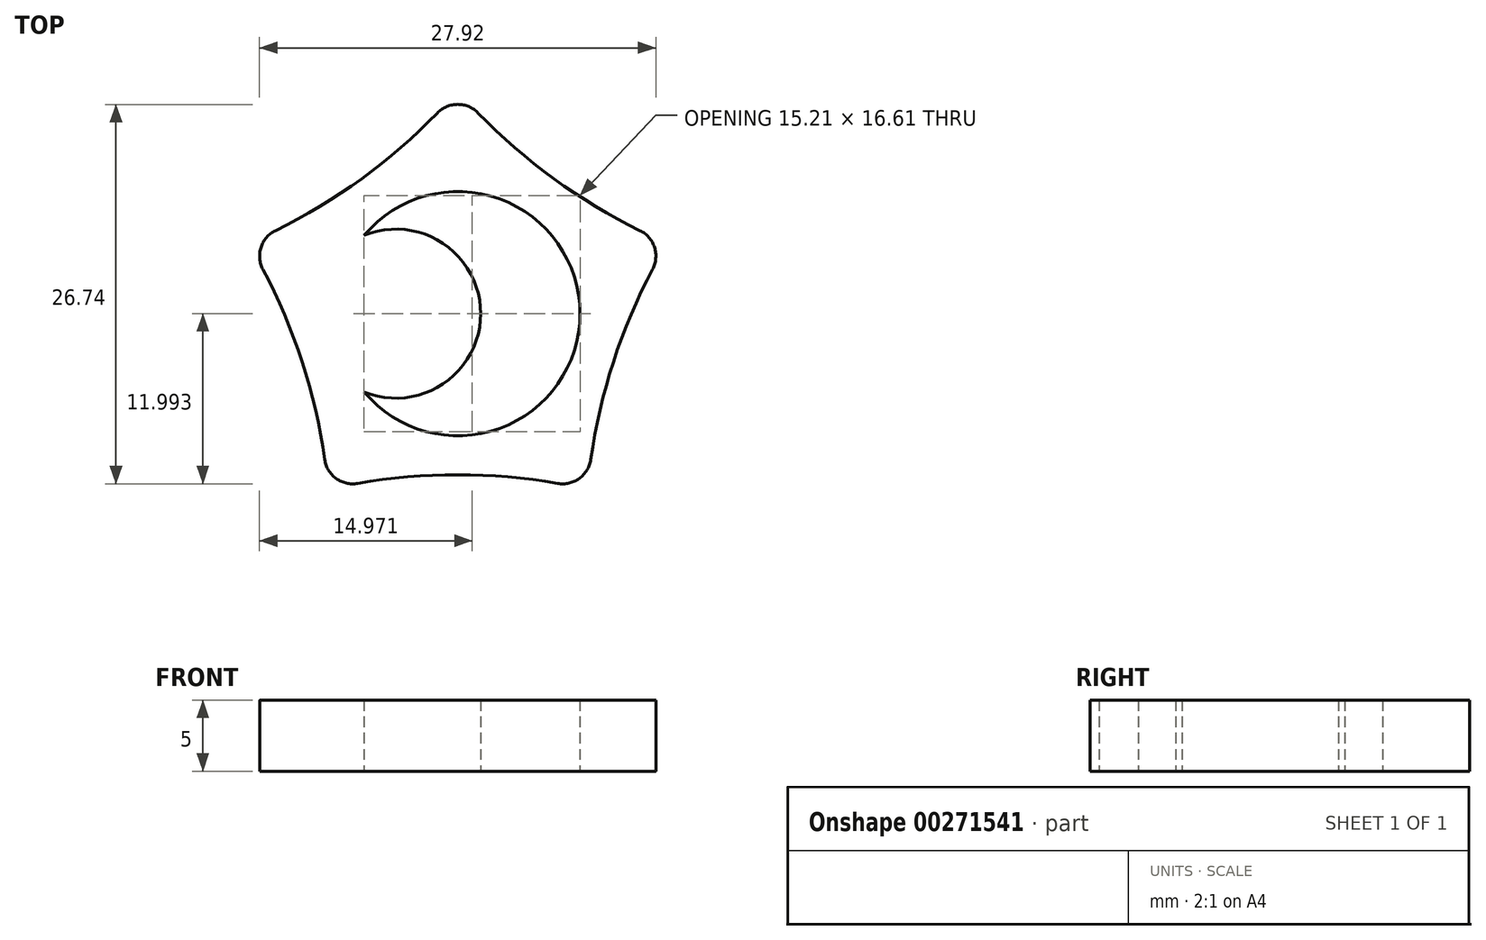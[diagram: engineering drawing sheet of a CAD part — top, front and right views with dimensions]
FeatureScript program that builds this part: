
annotation { "Feature Type Name" : "Feature", "Feature Type Description" : "" }
export const myFeature = defineFeature(function(context is Context, id is Id, definition is map)
    precondition{}
    {
        {
            var Q0;
            Q0=qCreatedBy(makeId("Top.planeOp"),FACE);
            var sketch = newSketch(context, id + "F0", { "sketchPlane" : qUnion([Q0])});
            skCircle(sketch, "E0.cCircle", {"center": v(0, 0) * mm, "radius": 12.56 * mm, "construction": true});
            skLineSegment(sketch, "E0.0", {"start": v(9.12, -12.56) * mm, "end": v(-9.12, -12.56) * mm});
            skLineSegment(sketch, "E0.1", {"start": v(-9.13, -12.56) * mm, "end": v(-14.76, 4.8) * mm});
            skLineSegment(sketch, "E0.2", {"start": v(-14.76, 4.8) * mm, "end": v(0, 15.52) * mm});
            skLineSegment(sketch, "E0.3", {"start": v(0, 15.52) * mm, "end": v(14.76, 4.8) * mm});
            skLineSegment(sketch, "E0.4", {"start": v(14.76, 4.8) * mm, "end": v(9.12, -12.56) * mm});
            skPoint(sketch, "E0.0.midPoint", {"position": v(0, -12.56) * mm});
            skArc(sketch, "E1", {"start": v(-6.6, -5.7) * mm, "mid": v(8.62, -0.18) * mm, "end": v(-6.6, 5.34) * mm});
            skArc(sketch, "E2", {"start": v(-6.6, -5.7) * mm, "mid": v(1.61, -0.18) * mm, "end": v(-6.6, 5.34) * mm});
            skArc(sketch, "E3", {"start": v(-9.13, -12.56) * mm, "mid": v(-10.97, -3.56) * mm, "end": v(-14.76, 4.8) * mm});
            skArc(sketch, "E4", {"start": v(-14.76, 4.8) * mm, "mid": v(-6.78, 9.33) * mm, "end": v(0, 15.52) * mm});
            skArc(sketch, "E5", {"start": v(0, 15.52) * mm, "mid": v(6.78, 9.33) * mm, "end": v(14.76, 4.8) * mm});
            skArc(sketch, "E6", {"start": v(14.76, 4.8) * mm, "mid": v(10.97, -3.56) * mm, "end": v(9.13, -12.56) * mm});
            skArc(sketch, "E7", {"start": v(9.13, -12.56) * mm, "mid": v(0, -11.53) * mm, "end": v(-9.13, -12.56) * mm});
            skSolve(sketch);
        }
        {
            var Q0;
            Q0=makeQuery(id+"F0.imprint","IMPRINT",FACE,{"disambiguationData":[TD([[makeQuery(id+"F0.imprint","IMPRINT",EDGE,{"derivedFrom":sQuery(id+"F0.wireOp",EDGE,"E1")}),-1.0]])]});
            extrude(context, id + "F1", {"entities" : qUnion([Q0]), "depth" : 5 * mm});
        }
        {
            var Q0;
            Q0=makeQuery(id+"F1.opExtrude","SWEPT_EDGE",EDGE,{"disambiguationData":[OSD([sQuery(id+"F0.wireOp",EDGE,"E0.1"),sQuery(id+"F0.wireOp",EDGE,"E0.2"),sQuery(id+"F0.wireOp",EDGE,"E3"),sQuery(id+"F0.wireOp",EDGE,"E4")])]});
            var Q1;
            Q1=makeQuery(id+"F1.opExtrude","SWEPT_EDGE",EDGE,{"disambiguationData":[OSD([sQuery(id+"F0.wireOp",EDGE,"E0.2"),sQuery(id+"F0.wireOp",EDGE,"E0.3"),sQuery(id+"F0.wireOp",EDGE,"E4"),sQuery(id+"F0.wireOp",EDGE,"E5")])]});
            var Q2;
            Q2=makeQuery(id+"F1.opExtrude","SWEPT_EDGE",EDGE,{"disambiguationData":[OSD([sQuery(id+"F0.wireOp",EDGE,"E0.3"),sQuery(id+"F0.wireOp",EDGE,"E0.4"),sQuery(id+"F0.wireOp",EDGE,"E5"),sQuery(id+"F0.wireOp",EDGE,"E6")])]});
            var Q3;
            Q3=makeQuery(id+"F1.opExtrude","SWEPT_EDGE",EDGE,{"disambiguationData":[OSD([sQuery(id+"F0.wireOp",EDGE,"E0.0"),sQuery(id+"F0.wireOp",EDGE,"E0.4"),sQuery(id+"F0.wireOp",EDGE,"E6"),sQuery(id+"F0.wireOp",EDGE,"E7")])]});
            var Q4;
            Q4=makeQuery(id+"F1.opExtrude","SWEPT_EDGE",EDGE,{"disambiguationData":[OSD([sQuery(id+"F0.wireOp",EDGE,"E0.0"),sQuery(id+"F0.wireOp",EDGE,"E0.1"),sQuery(id+"F0.wireOp",EDGE,"E3"),sQuery(id+"F0.wireOp",EDGE,"E7")])]});
            fillet(context, id + "F2", {"entities" : qUnion([Q0, Q1, Q2, Q3, Q4]), "radius" : 2 * mm, "tangentPropagation" : true, "allowEdgeOverflow" : false});
        }
    });
